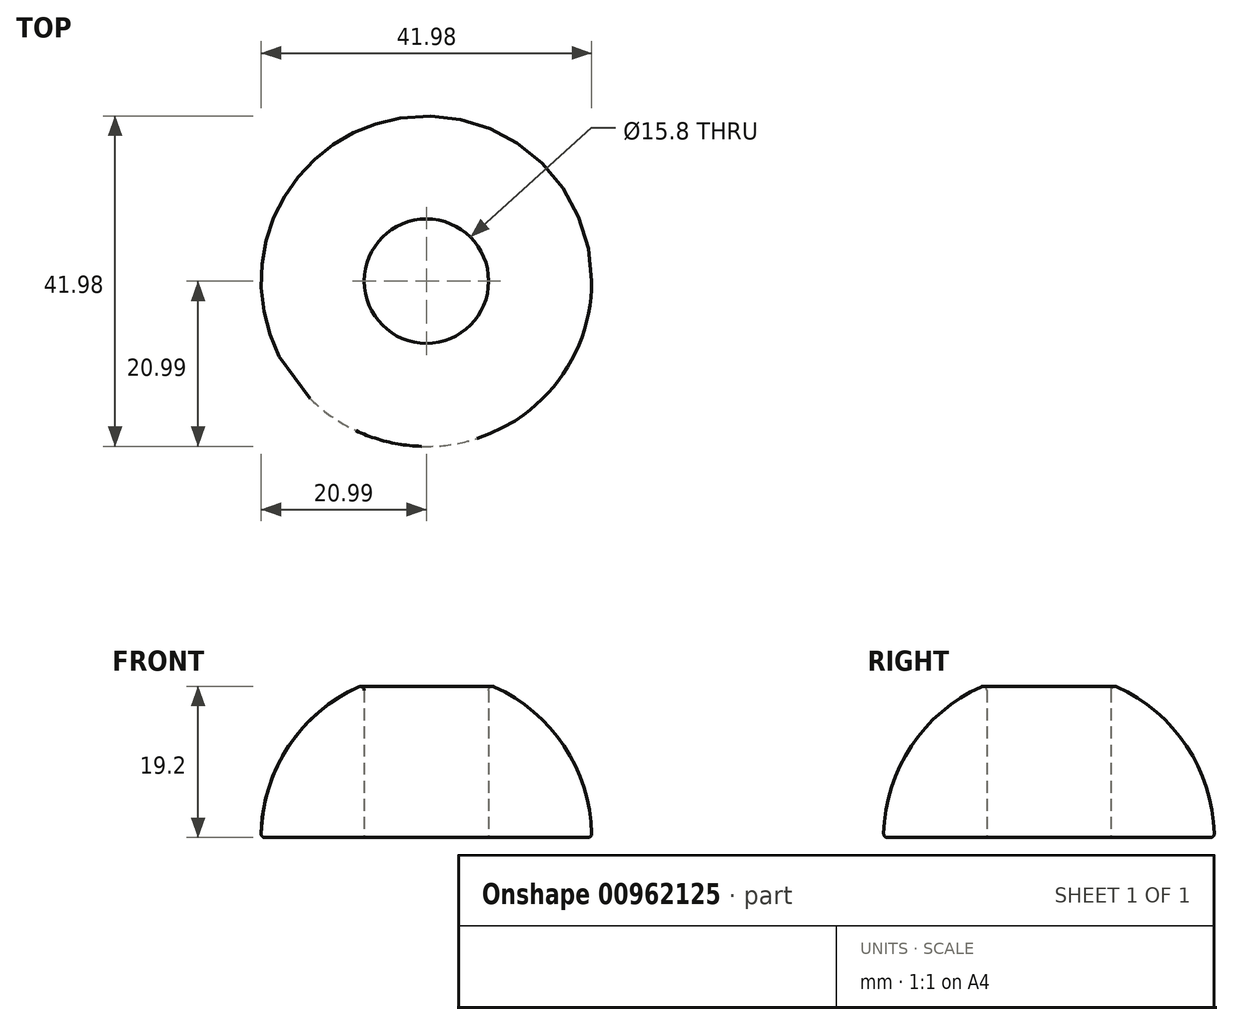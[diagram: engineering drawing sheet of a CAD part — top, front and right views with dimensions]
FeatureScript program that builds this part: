
annotation { "Feature Type Name" : "Feature", "Feature Type Description" : "" }
export const myFeature = defineFeature(function(context is Context, id is Id, definition is map)
    precondition{}
    {
        {
            assignVariable(context, id + "F0", {"variableType" : VariableType.LENGTH, "name" : "fillet", "lengthValue" : 0.5 * mm});
        }
        {
            var Q0;
            Q0=qCreatedBy(makeId("Front.planeOp"),FACE);
            var sketch = newSketch(context, id + "F1", { "sketchPlane" : qUnion([Q0])});
            skLineSegment(sketch, "E0", {"start": v(-21, 0) * mm, "end": v(0, 0) * mm});
            skLineSegment(sketch, "E1", {"start": v(0, 0) * mm, "end": v(0, 21) * mm});
            skArc(sketch, "E2", {"start": v(0, 21) * mm, "mid": v(-14.85, 14.85) * mm, "end": v(-21, 0) * mm});
            skSolve(sketch);
        }
        {
            var Q0;
            Q0=makeQuery(id+"F1.imprint","IMPRINT",FACE,{"disambiguationData":[TD([[makeQuery(id+"F1.imprint","IMPRINT",EDGE,{"derivedFrom":sQuery(id+"F1.wireOp",EDGE,"E0")}),1.0]])]});
            var Q1;
            Q1=sQuery(id+"F1.wireOp",EDGE,"E1");
            revolve(context, id + "F2", {"surfaceOperationType" : NewSurfaceOperationType.NEW, "entities" : qUnion([Q0]), "axis" : qUnion([Q1]), "revolveType" : RevolveType.FULL});
        }
        {
            var Q0;
            Q0=qCreatedBy(makeId("Top.planeOp"),FACE);
            var sketch = newSketch(context, id + "F3", { "sketchPlane" : qUnion([Q0])});
            skCircle(sketch, "E3", {"center": v(0, 0) * mm, "radius": 7.9 * mm});
            skSolve(sketch);
        }
        {
            var Q0;
            Q0=makeQuery(id+"F3.imprint","IMPRINT",FACE,{"disambiguationData":[TD([[makeQuery(id+"F3.imprint","IMPRINT",EDGE,{"derivedFrom":sQuery(id+"F3.wireOp",EDGE,"E3")}),1.0]])]});
            extrude(context, id + "F4", {"entities" : qUnion([Q0]), "operationType" : NewBodyOperationType.REMOVE, "endBound" : BoundingType.THROUGH_ALL, "depth" : 25 * mm, "offsetDistance" : 25 * mm});
        }
        {
            var Q0;
            Q0=makeQuery(id+"F2.opRevolve","SWEPT_EDGE",EDGE,{"disambiguationData":[OSD([sQuery(id+"F1.wireOp",EDGE,"E0"),sQuery(id+"F1.wireOp",EDGE,"E2")])]});
            var Q1;
            Q1=makeQuery(id+"F4.boolean.opBoolean","COPY",EDGE,{"derivedFrom":makeQuery(id+"F4.opExtrude","CAP_EDGE",EDGE,{"disambiguationData":[OSD([sQuery(id+"F3.wireOp",EDGE,"E3")])],"isStart":true})});
            var Q2;
            Q2=makeQuery(id+"F4.boolean.opBoolean","INTERSECT",EDGE,{"derivedFrom":[makeQuery(id+"F2.opRevolve","SWEPT_FACE",FACE,{"disambiguationData":[OSD([sQuery(id+"F1.wireOp",EDGE,"E2")])]}),makeQuery(id+"F4.opExtrude","SWEPT_FACE",FACE,{"disambiguationData":[OSD([sQuery(id+"F3.wireOp",EDGE,"E3")])]})]});
            fillet(context, id + "F5", {"entities" : qUnion([Q0, Q1, Q2]), "radius" : getVariable(context, 'fillet'), "tangentPropagation" : true, "allowEdgeOverflow" : false});
        }
    });
